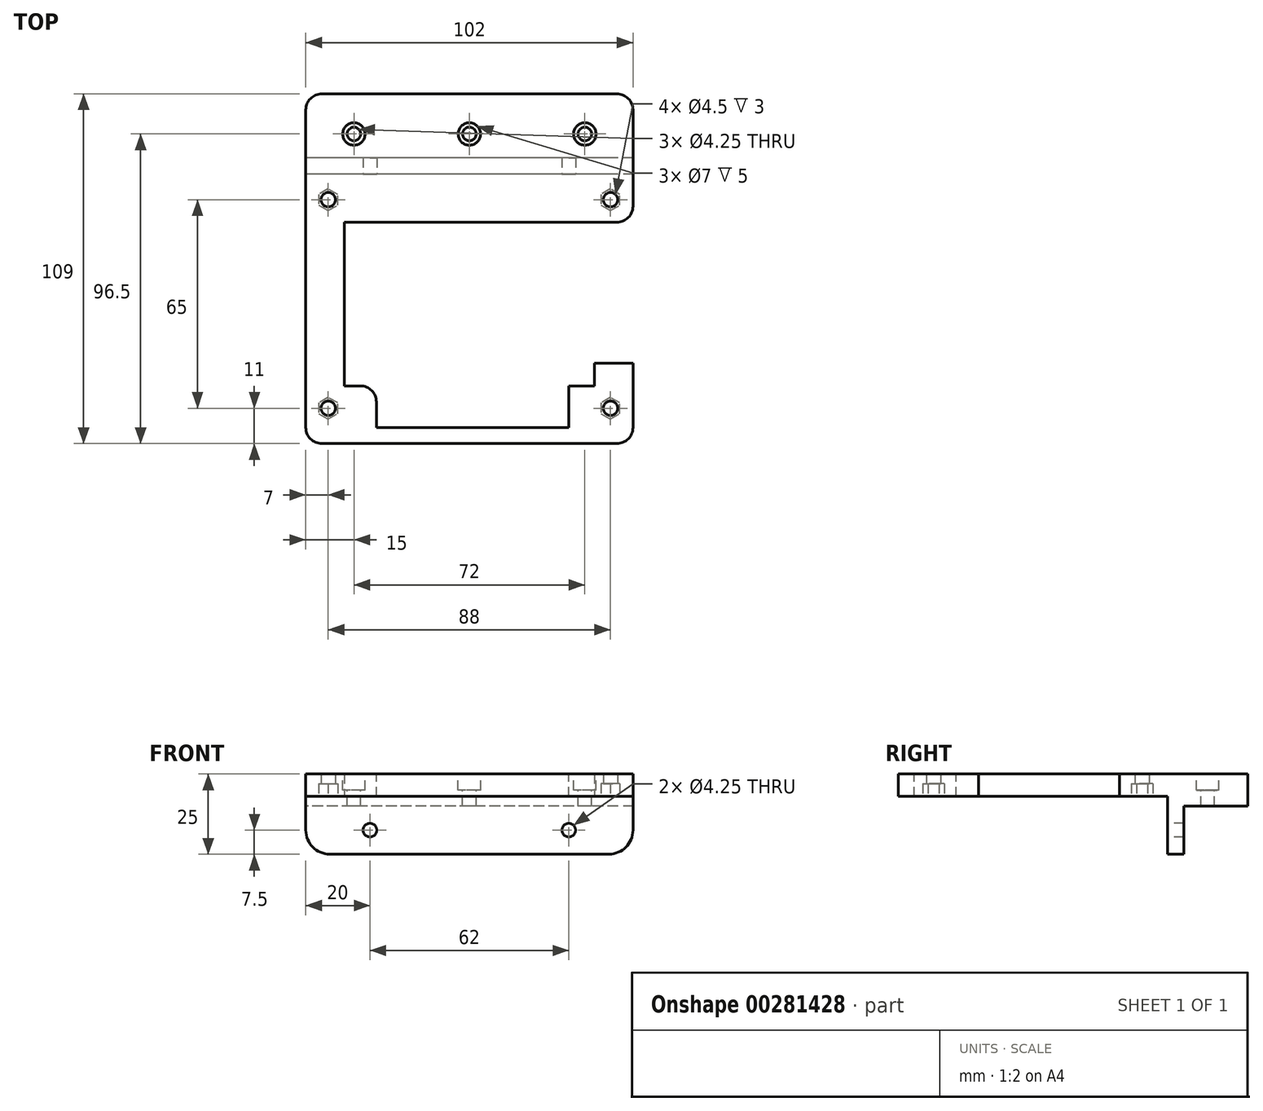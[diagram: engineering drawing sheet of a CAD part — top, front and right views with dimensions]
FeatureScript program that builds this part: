
annotation { "Feature Type Name" : "Feature", "Feature Type Description" : "" }
export const myFeature = defineFeature(function(context is Context, id is Id, definition is map)
    precondition{}
    {
        {
            var Q0;
            Q0=qCreatedBy(makeId("Top.planeOp"),FACE);
            var sketch = newSketch(context, id + "F0", { "sketchPlane" : qUnion([Q0])});
            skLineSegment(sketch, "E0.rect.bottom", {"start": v(44, -32.5) * mm, "end": v(-44, -32.5) * mm, "construction": true});
            skLineSegment(sketch, "E0.rect.top", {"start": v(44, 32.5) * mm, "end": v(-44, 32.5) * mm, "construction": true});
            skLineSegment(sketch, "E0.rect.left", {"start": v(44, -32.5) * mm, "end": v(44, 32.5) * mm, "construction": true});
            skLineSegment(sketch, "E0.rect.right", {"start": v(-44, -32.5) * mm, "end": v(-44, 32.5) * mm, "construction": true});
            skPoint(sketch, "E0.rect.middle", {"position": v(0, 0) * mm});
            skCircle(sketch, "E1", {"center": v(-44, 32.5) * mm, "radius": 2.25 * mm});
            skCircle(sketch, "E2", {"center": v(44, 32.5) * mm, "radius": 2.25 * mm});
            skCircle(sketch, "E3", {"center": v(-44, -32.5) * mm, "radius": 2.25 * mm});
            skCircle(sketch, "E4", {"center": v(44, -32.5) * mm, "radius": 2.25 * mm});
            skLineSegment(sketch, "E5.rect.bottom", {"start": v(39, -25.5) * mm, "end": v(-39, -25.5) * mm});
            skLineSegment(sketch, "E5.rect.top", {"start": v(39, 25.5) * mm, "end": v(-39, 25.5) * mm});
            skLineSegment(sketch, "E5.rect.left", {"start": v(39, -25.5) * mm, "end": v(39, 25.5) * mm});
            skLineSegment(sketch, "E5.rect.right", {"start": v(-39, -25.5) * mm, "end": v(-39, 25.5) * mm});
            skLineSegment(sketch, "E6", {"start": v(-51, -43.5) * mm, "end": v(51, -43.5) * mm});
            skLineSegment(sketch, "E7", {"start": v(51, -43.5) * mm, "end": v(51, 40.5) * mm});
            skLineSegment(sketch, "E8", {"start": v(51, 40.5) * mm, "end": v(-51, 40.5) * mm});
            skLineSegment(sketch, "E9", {"start": v(-51, 40.5) * mm, "end": v(-51, -43.5) * mm});
            skSolve(sketch);
        }
        {
            var Q0;
            Q0=qSketchRegion(id+"F0",true);
            extrude(context, id + "F1", {"entities" : qUnion([Q0]), "depth" : 15 * mm});
        }
        {
            var Q0;
            Q0=makeQuery(id+"F1.opExtrude","CAP_FACE",FACE,{"disambiguationData":[OSD([sQuery(id+"F0.wireOp",EDGE,"E1"),sQuery(id+"F0.wireOp",EDGE,"E2"),sQuery(id+"F0.wireOp",EDGE,"E3"),sQuery(id+"F0.wireOp",EDGE,"E4"),sQuery(id+"F0.wireOp",EDGE,"E5.rect.bottom"),sQuery(id+"F0.wireOp",EDGE,"E5.rect.top"),sQuery(id+"F0.wireOp",EDGE,"E5.rect.left"),sQuery(id+"F0.wireOp",EDGE,"E5.rect.right"),sQuery(id+"F0.wireOp",EDGE,"E6"),sQuery(id+"F0.wireOp",EDGE,"E7"),sQuery(id+"F0.wireOp",EDGE,"E8"),sQuery(id+"F0.wireOp",EDGE,"E9")])],"isStart":true});
            var sketch = newSketch(context, id + "F2", { "sketchPlane" : qUnion([Q0])});
            skCircle(sketch, "E10.cCircle", {"center": v(-44, 32.5) * mm, "radius": 2.92 * mm, "construction": true});
            skLineSegment(sketch, "E10.0", {"start": v(-41.08, 34.19) * mm, "end": v(-41.08, 30.81) * mm});
            skLineSegment(sketch, "E10.1", {"start": v(-41.08, 30.81) * mm, "end": v(-44, 29.12) * mm});
            skLineSegment(sketch, "E10.2", {"start": v(-44, 29.12) * mm, "end": v(-46.93, 30.81) * mm});
            skLineSegment(sketch, "E10.3", {"start": v(-46.93, 30.81) * mm, "end": v(-46.93, 34.19) * mm});
            skLineSegment(sketch, "E10.4", {"start": v(-46.93, 34.19) * mm, "end": v(-44, 35.88) * mm});
            skLineSegment(sketch, "E10.5", {"start": v(-44, 35.88) * mm, "end": v(-41.08, 34.19) * mm});
            skPoint(sketch, "E10.0.midPoint", {"position": v(-41.08, 32.5) * mm});
            skCircle(sketch, "E11.cCircle", {"center": v(44, 32.5) * mm, "radius": 2.92 * mm, "construction": true});
            skLineSegment(sketch, "E11.0", {"start": v(41.08, 30.81) * mm, "end": v(41.08, 34.19) * mm});
            skLineSegment(sketch, "E11.1", {"start": v(41.08, 34.19) * mm, "end": v(44, 35.88) * mm});
            skLineSegment(sketch, "E11.2", {"start": v(44, 35.88) * mm, "end": v(46.93, 34.19) * mm});
            skLineSegment(sketch, "E11.3", {"start": v(46.92, 34.19) * mm, "end": v(46.92, 30.81) * mm});
            skLineSegment(sketch, "E11.4", {"start": v(46.93, 30.81) * mm, "end": v(44, 29.12) * mm});
            skLineSegment(sketch, "E11.5", {"start": v(44, 29.12) * mm, "end": v(41.08, 30.81) * mm});
            skPoint(sketch, "E11.0.midPoint", {"position": v(41.08, 32.5) * mm});
            skCircle(sketch, "E12.cCircle", {"center": v(44, -32.5) * mm, "radius": 2.92 * mm, "construction": true});
            skLineSegment(sketch, "E12.0", {"start": v(41.08, -34.19) * mm, "end": v(41.08, -30.81) * mm});
            skLineSegment(sketch, "E12.1", {"start": v(41.08, -30.81) * mm, "end": v(44, -29.12) * mm});
            skLineSegment(sketch, "E12.2", {"start": v(44, -29.12) * mm, "end": v(46.93, -30.81) * mm});
            skLineSegment(sketch, "E12.3", {"start": v(46.93, -30.81) * mm, "end": v(46.93, -34.19) * mm});
            skLineSegment(sketch, "E12.4", {"start": v(46.93, -34.19) * mm, "end": v(44, -35.88) * mm});
            skLineSegment(sketch, "E12.5", {"start": v(44, -35.88) * mm, "end": v(41.08, -34.19) * mm});
            skPoint(sketch, "E12.0.midPoint", {"position": v(41.08, -32.5) * mm});
            skCircle(sketch, "E13.cCircle", {"center": v(-44, -32.5) * mm, "radius": 2.92 * mm, "construction": true});
            skLineSegment(sketch, "E13.0", {"start": v(-41.08, -30.81) * mm, "end": v(-41.08, -34.19) * mm});
            skLineSegment(sketch, "E13.1", {"start": v(-41.08, -34.19) * mm, "end": v(-44, -35.88) * mm});
            skLineSegment(sketch, "E13.2", {"start": v(-44, -35.88) * mm, "end": v(-46.93, -34.19) * mm});
            skLineSegment(sketch, "E13.3", {"start": v(-46.93, -34.19) * mm, "end": v(-46.93, -30.81) * mm});
            skLineSegment(sketch, "E13.4", {"start": v(-46.93, -30.81) * mm, "end": v(-44, -29.12) * mm});
            skLineSegment(sketch, "E13.5", {"start": v(-44, -29.12) * mm, "end": v(-41.08, -30.81) * mm});
            skPoint(sketch, "E13.0.midPoint", {"position": v(-41.08, -32.5) * mm});
            skSolve(sketch);
        }
        {
            var Q0;
            Q0=qSketchRegion(id+"F2",true);
            extrude(context, id + "F3", {"entities" : qUnion([Q0]), "operationType" : NewBodyOperationType.REMOVE, "oppositeDirection" : true, "depth" : 4 * mm});
        }
        {
            var Q0;
            Q0=makeQuery(id+"F1.opExtrude","CAP_FACE",FACE,{"disambiguationData":[OSD([sQuery(id+"F0.wireOp",EDGE,"E1"),sQuery(id+"F0.wireOp",EDGE,"E2"),sQuery(id+"F0.wireOp",EDGE,"E3"),sQuery(id+"F0.wireOp",EDGE,"E4"),sQuery(id+"F0.wireOp",EDGE,"E5.rect.bottom"),sQuery(id+"F0.wireOp",EDGE,"E5.rect.top"),sQuery(id+"F0.wireOp",EDGE,"E5.rect.left"),sQuery(id+"F0.wireOp",EDGE,"E5.rect.right"),sQuery(id+"F0.wireOp",EDGE,"E6"),sQuery(id+"F0.wireOp",EDGE,"E7"),sQuery(id+"F0.wireOp",EDGE,"E8"),sQuery(id+"F0.wireOp",EDGE,"E9")])],"isStart":false});
            var sketch = newSketch(context, id + "F4", { "sketchPlane" : qUnion([Q0])});
            skLineSegment(sketch, "E14", {"start": v(39, -18.5) * mm, "end": v(51, -18.5) * mm});
            skLineSegment(sketch, "E15", {"start": v(51, -18.5) * mm, "end": v(51, 25.5) * mm});
            skLineSegment(sketch, "E16", {"start": v(51, 25.5) * mm, "end": v(39, 25.5) * mm});
            skLineSegment(sketch, "E17", {"start": v(39, 25.5) * mm, "end": v(39, -18.5) * mm});
            skLineSegment(sketch, "E18", {"start": v(31, -25.5) * mm, "end": v(31, -38.5) * mm});
            skLineSegment(sketch, "E19", {"start": v(31, -38.5) * mm, "end": v(-29, -38.5) * mm});
            skLineSegment(sketch, "E20", {"start": v(-29, -38.5) * mm, "end": v(-29, -25.5) * mm});
            skLineSegment(sketch, "E21", {"start": v(-29, -25.5) * mm, "end": v(31, -25.5) * mm});
            skSolve(sketch);
        }
        {
            var Q0;
            Q0=qSketchRegion(id+"F4",true);
            extrude(context, id + "F5", {"entities" : qUnion([Q0]), "operationType" : NewBodyOperationType.REMOVE, "endBound" : BoundingType.THROUGH_ALL, "oppositeDirection" : true, "depth" : 5 * mm});
        }
        {
            var Q0;
            Q0=makeQuery(id+"F1.opExtrude","CAP_FACE",FACE,{"disambiguationData":[OSD([sQuery(id+"F0.wireOp",EDGE,"E1"),sQuery(id+"F0.wireOp",EDGE,"E2"),sQuery(id+"F0.wireOp",EDGE,"E3"),sQuery(id+"F0.wireOp",EDGE,"E4"),sQuery(id+"F0.wireOp",EDGE,"E5.rect.bottom"),sQuery(id+"F0.wireOp",EDGE,"E5.rect.top"),sQuery(id+"F0.wireOp",EDGE,"E5.rect.left"),sQuery(id+"F0.wireOp",EDGE,"E5.rect.right"),sQuery(id+"F0.wireOp",EDGE,"E6"),sQuery(id+"F0.wireOp",EDGE,"E7"),sQuery(id+"F0.wireOp",EDGE,"E8"),sQuery(id+"F0.wireOp",EDGE,"E9")])],"isStart":false});
            var sketch = newSketch(context, id + "F6", { "sketchPlane" : qUnion([Q0])});
            skLineSegment(sketch, "E22.rect.bottom", {"start": v(-51, 40.5) * mm, "end": v(51, 40.5) * mm});
            skLineSegment(sketch, "E22.rect.top", {"start": v(-51, -43.5) * mm, "end": v(51, -43.5) * mm});
            skLineSegment(sketch, "E22.rect.left", {"start": v(-51, 40.5) * mm, "end": v(-51, -43.5) * mm});
            skLineSegment(sketch, "E22.rect.right", {"start": v(51, 40.5) * mm, "end": v(51, -43.5) * mm});
            skPoint(sketch, "E22.rect.middle", {"position": v(0, -1.5) * mm});
            skSolve(sketch);
        }
        {
            var Q0;
            Q0=qSketchRegion(id+"F6",true);
            extrude(context, id + "F7", {"entities" : qUnion([Q0]), "operationType" : NewBodyOperationType.REMOVE, "oppositeDirection" : true, "depth" : 8 * mm});
        }
        {
            var Q0;
            Q0=makeQuery(id+"F7.boolean.opBoolean","COPY",FACE,{"derivedFrom":makeQuery(id+"F7.opExtrude","CAP_FACE",FACE,{"disambiguationData":[OSD([sQuery(id+"F6.wireOp",EDGE,"E22.rect.bottom"),sQuery(id+"F6.wireOp",EDGE,"E22.rect.top"),sQuery(id+"F6.wireOp",EDGE,"E22.rect.left"),sQuery(id+"F6.wireOp",EDGE,"E22.rect.right")])],"isStart":false})});
            var sketch = newSketch(context, id + "F8", { "sketchPlane" : qUnion([Q0])});
            skLineSegment(sketch, "E23.bottom", {"start": v(51, 40.5) * mm, "end": v(-51, 40.5) * mm});
            skLineSegment(sketch, "E23.top", {"start": v(51, 65.5) * mm, "end": v(-51, 65.5) * mm});
            skLineSegment(sketch, "E23.left", {"start": v(51, 40.5) * mm, "end": v(51, 65.5) * mm});
            skLineSegment(sketch, "E23.right", {"start": v(-51, 40.5) * mm, "end": v(-51, 65.5) * mm});
            skPoint(sketch, "E23.middle", {"position": v(0, 53) * mm});
            skCircle(sketch, "E24", {"center": v(-36, 53) * mm, "radius": 2.12 * mm});
            skCircle(sketch, "E25", {"center": v(0, 53) * mm, "radius": 2.12 * mm});
            skCircle(sketch, "E26.MirrorC", {"center": v(36, 53) * mm, "radius": 2.12 * mm});
            skSolve(sketch);
        }
        {
            var Q0;
            Q0=qSketchRegion(id+"F8",true);
            extrude(context, id + "F9", {"entities" : qUnion([Q0]), "operationType" : NewBodyOperationType.ADD, "oppositeDirection" : true, "depth" : 10 * mm});
        }
        {
            var Q0;
            Q0=makeQuery(id+"F9.boolean.opBoolean","MERGE",FACE,{"derivedFrom":[makeQuery(id+"F7.boolean.opBoolean","COPY",FACE,{"derivedFrom":makeQuery(id+"F7.opExtrude","CAP_FACE",FACE,{"disambiguationData":[OSD([sQuery(id+"F6.wireOp",EDGE,"E22.rect.bottom"),sQuery(id+"F6.wireOp",EDGE,"E22.rect.top"),sQuery(id+"F6.wireOp",EDGE,"E22.rect.left"),sQuery(id+"F6.wireOp",EDGE,"E22.rect.right")])],"isStart":false})}),makeQuery(id+"F9.opExtrude","CAP_FACE",FACE,{"disambiguationData":[OSD([sQuery(id+"F8.wireOp",EDGE,"E23.bottom"),sQuery(id+"F8.wireOp",EDGE,"E23.top"),sQuery(id+"F8.wireOp",EDGE,"E23.left"),sQuery(id+"F8.wireOp",EDGE,"E23.right"),sQuery(id+"F8.wireOp",EDGE,"E24"),sQuery(id+"F8.wireOp",EDGE,"E25"),sQuery(id+"F8.wireOp",EDGE,"E26.MirrorC")])],"isStart":true})]});
            var sketch = newSketch(context, id + "F10", { "sketchPlane" : qUnion([Q0])});
            skCircle(sketch, "E27", {"center": v(36, 53) * mm, "radius": 3.5 * mm});
            skCircle(sketch, "E28", {"center": v(0, 53) * mm, "radius": 3.5 * mm});
            skCircle(sketch, "E29", {"center": v(-36, 53) * mm, "radius": 3.5 * mm});
            skSolve(sketch);
        }
        {
            var Q0;
            Q0=qSketchRegion(id+"F10",true);
            extrude(context, id + "F11", {"entities" : qUnion([Q0]), "operationType" : NewBodyOperationType.REMOVE, "oppositeDirection" : true, "depth" : 5 * mm});
        }
        {
            var Q0;
            Q0=makeQuery(id+"F1.opExtrude","SWEPT_EDGE",EDGE,{"disambiguationData":[OSD([sQuery(id+"F0.wireOp",EDGE,"E8"),sQuery(id+"F0.wireOp",EDGE,"E9")])]});
            var Q1;
            Q1=makeQuery(id+"F1.opExtrude","SWEPT_EDGE",EDGE,{"disambiguationData":[OSD([sQuery(id+"F0.wireOp",EDGE,"E7"),sQuery(id+"F0.wireOp",EDGE,"E8")])]});
            var Q2;
            Q2=makeQuery(id+"F1.opExtrude","SWEPT_EDGE",EDGE,{"disambiguationData":[OSD([sQuery(id+"F0.wireOp",EDGE,"E6"),sQuery(id+"F0.wireOp",EDGE,"E9")])]});
            var Q3;
            Q3=makeQuery(id+"F1.opExtrude","SWEPT_EDGE",EDGE,{"disambiguationData":[OSD([sQuery(id+"F0.wireOp",EDGE,"E6"),sQuery(id+"F0.wireOp",EDGE,"E7")])]});
            var Q4;
            Q4=makeQuery(id+"F5.boolean.opBoolean","COPY",EDGE,{"derivedFrom":makeQuery(id+"F5.opExtrude","SWEPT_EDGE",EDGE,{"disambiguationData":[OSD([sQuery(id+"F0.wireOp",EDGE,"E7"),sQuery(id+"F4.wireOp",EDGE,"E15"),sQuery(id+"F4.wireOp",EDGE,"E16")])]})});
            var Q5;
            Q5=makeQuery(id+"F5.boolean.opBoolean","COPY",EDGE,{"derivedFrom":makeQuery(id+"F5.opExtrude","SWEPT_EDGE",EDGE,{"disambiguationData":[OSD([sQuery(id+"F0.wireOp",EDGE,"E7"),sQuery(id+"F4.wireOp",EDGE,"E14"),sQuery(id+"F4.wireOp",EDGE,"E15")])]})});
            var Q6;
            Q6=makeQuery(id+"F5.boolean.opBoolean","COPY",EDGE,{"derivedFrom":makeQuery(id+"F5.opExtrude","SWEPT_EDGE",EDGE,{"disambiguationData":[OSD([sQuery(id+"F0.wireOp",EDGE,"E5.rect.left"),sQuery(id+"F4.wireOp",EDGE,"E16"),sQuery(id+"F4.wireOp",EDGE,"E17")])]})});
            var Q7;
            Q7=makeQuery(id+"F5.boolean.opBoolean","COPY",EDGE,{"derivedFrom":makeQuery(id+"F5.opExtrude","SWEPT_EDGE",EDGE,{"disambiguationData":[OSD([sQuery(id+"F0.wireOp",EDGE,"E5.rect.left"),sQuery(id+"F4.wireOp",EDGE,"E14"),sQuery(id+"F4.wireOp",EDGE,"E17")])]})});
            var Q8;
            Q8=makeQuery(id+"F5.boolean.opBoolean","COPY",EDGE,{"derivedFrom":makeQuery(id+"F5.opExtrude","SWEPT_EDGE",EDGE,{"disambiguationData":[OSD([sQuery(id+"F0.wireOp",EDGE,"E5.rect.bottom"),sQuery(id+"F4.wireOp",EDGE,"E18"),sQuery(id+"F4.wireOp",EDGE,"E21")])]})});
            var Q9;
            Q9=makeQuery(id+"F5.boolean.opBoolean","COPY",EDGE,{"derivedFrom":makeQuery(id+"F5.opExtrude","SWEPT_EDGE",EDGE,{"disambiguationData":[OSD([sQuery(id+"F0.wireOp",EDGE,"E5.rect.bottom"),sQuery(id+"F4.wireOp",EDGE,"E20"),sQuery(id+"F4.wireOp",EDGE,"E21")])]})});
            var Q10;
            Q10=makeQuery(id+"F9.opExtrude","SWEPT_EDGE",EDGE,{"disambiguationData":[OSD([sQuery(id+"F8.wireOp",EDGE,"E23.top"),sQuery(id+"F8.wireOp",EDGE,"E23.right")])]});
            var Q11;
            Q11=makeQuery(id+"F9.opExtrude","SWEPT_EDGE",EDGE,{"disambiguationData":[OSD([sQuery(id+"F8.wireOp",EDGE,"E23.top"),sQuery(id+"F8.wireOp",EDGE,"E23.left")])]});
            fillet(context, id + "F12", {"entities" : qUnion([Q0, Q1, Q2, Q3, Q4, Q5, Q6, Q7, Q8, Q9, Q10, Q11]), "radius" : 5 * mm, "tangentPropagation" : true, "allowEdgeOverflow" : false});
        }
        {
            var Q0;
            Q0=makeQuery(id+"F9.opExtrude","CAP_FACE",FACE,{"disambiguationData":[OSD([sQuery(id+"F8.wireOp",EDGE,"E23.bottom"),sQuery(id+"F8.wireOp",EDGE,"E23.top"),sQuery(id+"F8.wireOp",EDGE,"E23.left"),sQuery(id+"F8.wireOp",EDGE,"E23.right"),sQuery(id+"F8.wireOp",EDGE,"E24"),sQuery(id+"F8.wireOp",EDGE,"E25"),sQuery(id+"F8.wireOp",EDGE,"E26.MirrorC")])],"isStart":false});
            var sketch = newSketch(context, id + "F13", { "sketchPlane" : qUnion([Q0])});
            skLineSegment(sketch, "E30.bottom", {"start": v(51, -40.5) * mm, "end": v(-51, -40.5) * mm});
            skLineSegment(sketch, "E30.top", {"start": v(51, -45.5) * mm, "end": v(-51, -45.5) * mm});
            skLineSegment(sketch, "E30.left", {"start": v(51, -40.5) * mm, "end": v(51, -45.5) * mm});
            skLineSegment(sketch, "E30.right", {"start": v(-51, -40.5) * mm, "end": v(-51, -45.5) * mm});
            skPoint(sketch, "E30.middle", {"position": v(0, -43) * mm});
            skSolve(sketch);
        }
        {
            var Q0;
            Q0=qSketchRegion(id+"F13",true);
            extrude(context, id + "F14", {"entities" : qUnion([Q0]), "operationType" : NewBodyOperationType.ADD, "depth" : 15 * mm});
        }
        {
            var Q0;
            Q0=makeQuery(id+"F14.boolean.opBoolean","MERGE",FACE,{"derivedFrom":[makeQuery(id+"F9.opExtrude","SWEPT_FACE",FACE,{"disambiguationData":[OSD([sQuery(id+"F8.wireOp",EDGE,"E23.bottom")])]}),makeQuery(id+"F14.opExtrude","SWEPT_FACE",FACE,{"disambiguationData":[OSD([sQuery(id+"F13.wireOp",EDGE,"E30.bottom")])]})]});
            var sketch = newSketch(context, id + "F15", { "sketchPlane" : qUnion([Q0])});
            skCircle(sketch, "E31", {"center": v(-31, -10.5) * mm, "radius": 2.12 * mm});
            skCircle(sketch, "E32", {"center": v(31, -10.5) * mm, "radius": 2.12 * mm});
            skSolve(sketch);
        }
        {
            var Q0;
            Q0=qSketchRegion(id+"F15",true);
            extrude(context, id + "F16", {"entities" : qUnion([Q0]), "operationType" : NewBodyOperationType.REMOVE, "oppositeDirection" : true, "depth" : 25 * mm});
        }
        {
            var Q0;
            Q0=makeQuery(id+"F14.opExtrude","CAP_EDGE",EDGE,{"disambiguationData":[OSD([sQuery(id+"F13.wireOp",EDGE,"E30.right")])],"isStart":false});
            var Q1;
            Q1=makeQuery(id+"F14.opExtrude","CAP_EDGE",EDGE,{"disambiguationData":[OSD([sQuery(id+"F13.wireOp",EDGE,"E30.left")])],"isStart":false});
            fillet(context, id + "F17", {"entities" : qUnion([Q0, Q1]), "radius" : 7.5 * mm, "tangentPropagation" : true, "allowEdgeOverflow" : false});
        }
    });
